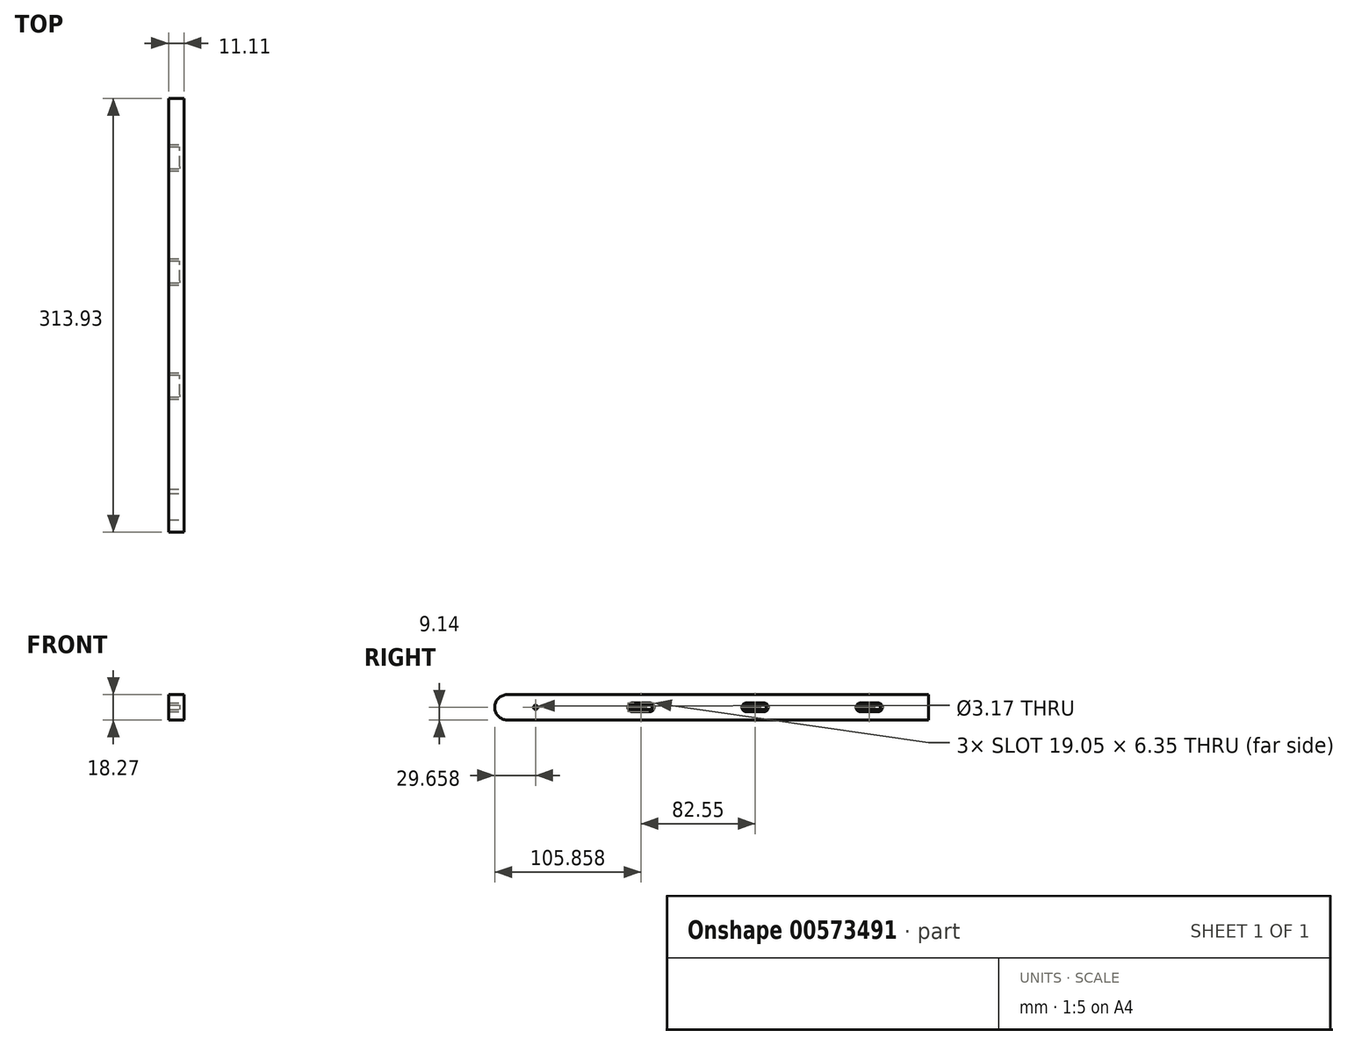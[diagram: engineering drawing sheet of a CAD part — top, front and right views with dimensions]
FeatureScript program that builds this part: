
annotation { "Feature Type Name" : "Feature", "Feature Type Description" : "" }
export const myFeature = defineFeature(function(context is Context, id is Id, definition is map)
    precondition{}
    {
        {
            var Q0;
            Q0=qCreatedBy(makeId("Right.planeOp"),FACE);
            var sketch = newSketch(context, id + "F0", { "sketchPlane" : qUnion([Q0])});
            skArc(sketch, "E0", {"start": v(0, 9.13) * mm, "mid": v(-9.13, 0) * mm, "end": v(0, -9.13) * mm});
            skLineSegment(sketch, "E1.bottom", {"start": v(0, 9.13) * mm, "end": v(304.8, 9.13) * mm});
            skLineSegment(sketch, "E1.top", {"start": v(0, -9.14) * mm, "end": v(304.8, -9.14) * mm});
            skLineSegment(sketch, "E1.right", {"start": v(304.8, 9.13) * mm, "end": v(304.8, -9.14) * mm});
            skLineSegment(sketch, "E2.trimOffspring", {"start": v(0, -9.13) * mm, "end": v(0, -9.14) * mm});
            skCircle(sketch, "E3", {"center": v(20.53, 0) * mm, "radius": 1.59 * mm});
            skLineSegment(sketch, "E4", {"start": v(90.38, 0) * mm, "end": v(103.08, 0) * mm});
            skLineSegment(sketch, "E5", {"start": v(172.93, 0) * mm, "end": v(185.63, 0) * mm});
            skLineSegment(sketch, "E6", {"start": v(255.48, 0) * mm, "end": v(268.18, 0) * mm});
            skArc(sketch, "E7.0.startCap", {"start": v(172.93, -1.59) * mm, "mid": v(171.34, 0) * mm, "end": v(172.93, 1.59) * mm});
            skArc(sketch, "E7.0.endCap", {"start": v(185.63, 1.59) * mm, "mid": v(187.22, 0) * mm, "end": v(185.63, -1.59) * mm});
            skLineSegment(sketch, "E7.0.left", {"start": v(172.93, 1.59) * mm, "end": v(185.63, 1.59) * mm});
            skLineSegment(sketch, "E7.0.right", {"start": v(172.93, -1.59) * mm, "end": v(185.63, -1.59) * mm});
            skArc(sketch, "E8.0.startCap", {"start": v(255.48, -1.59) * mm, "mid": v(253.9, 0) * mm, "end": v(255.48, 1.59) * mm});
            skArc(sketch, "E8.0.endCap", {"start": v(268.18, 1.59) * mm, "mid": v(269.77, 0) * mm, "end": v(268.18, -1.59) * mm});
            skLineSegment(sketch, "E8.0.left", {"start": v(255.48, 1.59) * mm, "end": v(268.18, 1.59) * mm});
            skLineSegment(sketch, "E8.0.right", {"start": v(255.48, -1.59) * mm, "end": v(268.18, -1.59) * mm});
            skArc(sketch, "E9.0.startCap", {"start": v(90.38, -1.59) * mm, "mid": v(88.8, 0) * mm, "end": v(90.38, 1.59) * mm});
            skArc(sketch, "E9.0.endCap", {"start": v(103.08, 1.59) * mm, "mid": v(104.67, 0) * mm, "end": v(103.08, -1.59) * mm});
            skLineSegment(sketch, "E9.0.left", {"start": v(90.38, 1.59) * mm, "end": v(103.08, 1.59) * mm});
            skLineSegment(sketch, "E9.0.right", {"start": v(90.38, -1.59) * mm, "end": v(103.08, -1.59) * mm});
            skArc(sketch, "E10.0.startCap", {"start": v(90.38, -3.18) * mm, "mid": v(87.2, 0) * mm, "end": v(90.38, 3.18) * mm});
            skArc(sketch, "E10.0.endCap", {"start": v(103.08, 3.18) * mm, "mid": v(106.25, 0) * mm, "end": v(103.08, -3.18) * mm});
            skLineSegment(sketch, "E10.0.left", {"start": v(90.38, 3.18) * mm, "end": v(103.08, 3.18) * mm});
            skLineSegment(sketch, "E10.0.right", {"start": v(90.38, -3.18) * mm, "end": v(103.08, -3.18) * mm});
            skArc(sketch, "E11.0.startCap", {"start": v(172.93, -3.18) * mm, "mid": v(169.75, 0) * mm, "end": v(172.93, 3.18) * mm});
            skArc(sketch, "E11.0.endCap", {"start": v(185.63, 3.18) * mm, "mid": v(188.8, 0) * mm, "end": v(185.63, -3.18) * mm});
            skLineSegment(sketch, "E11.0.left", {"start": v(172.93, 3.18) * mm, "end": v(185.63, 3.18) * mm});
            skLineSegment(sketch, "E11.0.right", {"start": v(172.93, -3.18) * mm, "end": v(185.63, -3.18) * mm});
            skArc(sketch, "E11.1.startCap", {"start": v(255.48, -3.18) * mm, "mid": v(252.3, 0) * mm, "end": v(255.48, 3.18) * mm});
            skArc(sketch, "E11.1.endCap", {"start": v(268.18, 3.18) * mm, "mid": v(271.35, 0) * mm, "end": v(268.18, -3.18) * mm});
            skLineSegment(sketch, "E11.1.left", {"start": v(255.48, 3.18) * mm, "end": v(268.18, 3.18) * mm});
            skLineSegment(sketch, "E11.1.right", {"start": v(255.48, -3.18) * mm, "end": v(268.18, -3.18) * mm});
            skSolve(sketch);
        }
        {
            var Q0;
            Q0=makeQuery(id+"F0.imprint","IMPRINT",FACE,{"disambiguationData":[TD([[makeQuery(id+"F0.imprint","IMPRINT",EDGE,{"derivedFrom":sQuery(id+"F0.wireOp",EDGE,"E0")}),1.0]])]});
            var Q1;
            Q1=makeQuery(id+"F0.imprint","IMPRINT",FACE,{"disambiguationData":[TD([[makeQuery(id+"F0.imprint","IMPRINT",EDGE,{"derivedFrom":sQuery(id+"F0.wireOp",EDGE,"E9.0.startCap")}),1.0]])]});
            var Q2;
            Q2=makeQuery(id+"F0.imprint","IMPRINT",FACE,{"disambiguationData":[TD([[makeQuery(id+"F0.imprint","IMPRINT",EDGE,{"derivedFrom":sQuery(id+"F0.wireOp",EDGE,"E8.0.startCap")}),1.0]])]});
            var Q3;
            Q3=makeQuery(id+"F0.imprint","IMPRINT",FACE,{"disambiguationData":[TD([[makeQuery(id+"F0.imprint","IMPRINT",EDGE,{"derivedFrom":sQuery(id+"F0.wireOp",EDGE,"E7.0.startCap")}),1.0]])]});
            extrude(context, id + "F1", {"entities" : qUnion([Q0, Q1, Q2, Q3]), "oppositeDirection" : true, "depth" : 11.1 * mm, "offsetDistance" : 25.4 * mm});
        }
        {
            var Q0;
            Q0=makeQuery(id+"F0.imprint","IMPRINT",FACE,{"disambiguationData":[TD([[makeQuery(id+"F0.imprint","IMPRINT",EDGE,{"derivedFrom":sQuery(id+"F0.wireOp",EDGE,"E9.0.startCap")}),1.0]])]});
            var Q1;
            Q1=makeQuery(id+"F0.imprint","IMPRINT",FACE,{"disambiguationData":[TD([[makeQuery(id+"F0.imprint","IMPRINT",EDGE,{"derivedFrom":sQuery(id+"F0.wireOp",EDGE,"E7.0.startCap")}),1.0]])]});
            var Q2;
            Q2=makeQuery(id+"F0.imprint","IMPRINT",FACE,{"disambiguationData":[TD([[makeQuery(id+"F0.imprint","IMPRINT",EDGE,{"derivedFrom":sQuery(id+"F0.wireOp",EDGE,"E8.0.startCap")}),1.0]])]});
            extrude(context, id + "F2", {"entities" : qUnion([Q0, Q1, Q2]), "operationType" : NewBodyOperationType.REMOVE, "oppositeDirection" : true, "depth" : 3.17 * mm, "offsetDistance" : 25.4 * mm});
        }
    });
